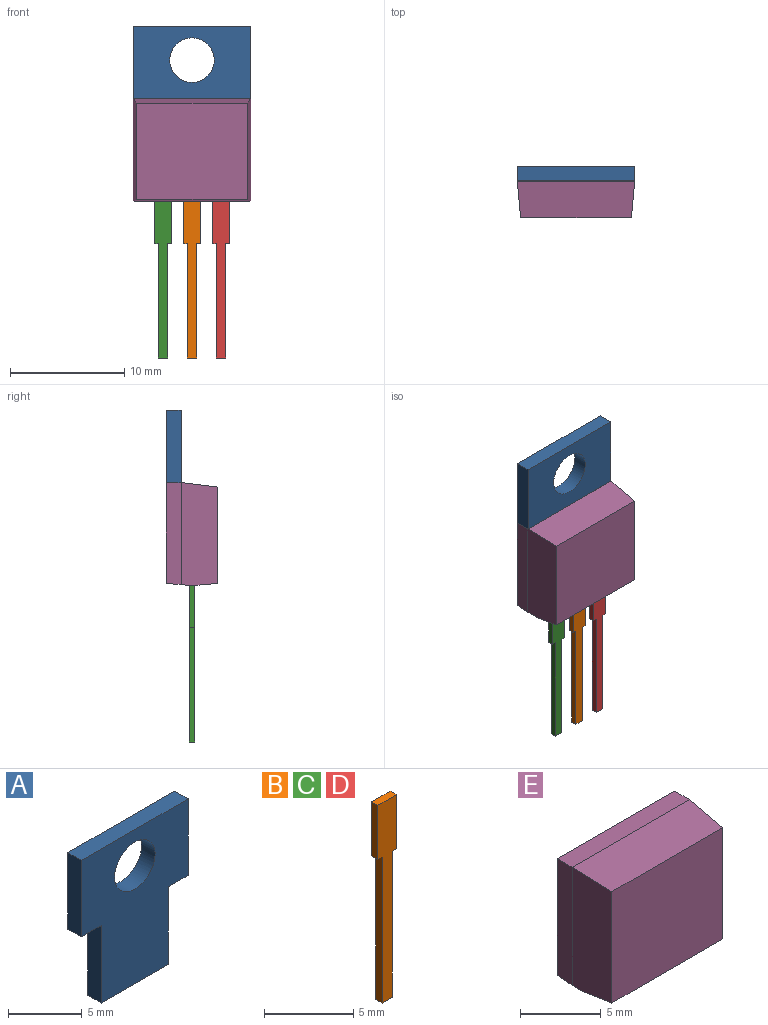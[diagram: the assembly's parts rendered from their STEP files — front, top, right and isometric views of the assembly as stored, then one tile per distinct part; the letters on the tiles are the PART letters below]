
ASSEMBLY  parts=5 mates=4
PART A: 11 faces, bbox 10.3x1.3x12.8 mm
  f0: plane 10.26x1.3mm, normal (0,0,1), area 13.3mm2, adj f1,f7,f8,f9
  f1: plane 6.35x1.3mm, normal (-1,0,0), area 8.3mm2, adj f0,f2,f8,f9
  f2: plane 1.91x1.3mm, normal (0,0,-1), area 2.5mm2, adj f1,f3,f8,f9
  f3: plane 6.45x1.3mm, normal (-1,0,0), area 8.4mm2, adj f2,f4,f8,f9
  f4: plane 6.44x1.3mm, normal (0,0,-1), area 8.4mm2, adj f3,f5,f8,f9
  f5: plane 6.45x1.3mm, normal (1,0,0), area 8.4mm2, adj f4,f6,f8,f9
  f6: plane 1.91x1.3mm, normal (0,0,-1), area 2.5mm2, adj f5,f7,f8,f9
  f7: plane 6.35x1.3mm, normal (1,0,0), area 8.3mm2, adj f0,f6,f8,f9
  f8: plane 12.8x10.26mm, normal (0,-1,0), area 94.8mm2, adj f0,f1,f2,f3,f4,f5,f6,f7
  f9: plane 12.8x10.26mm, normal (0,1,0), area 94.8mm2, adj f0,f1,f2,f3,f4,f5,f6,f7
  f10: cylinder r=1.95mm len=3.9mm, axis (0,1,0), area 15.9mm2, adj f8,f9
PART B: 10 faces, bbox 1.5x0.5x13.7 mm
  f0: plane 3.7x0.5mm, normal (-1,0,0), area 1.9mm2, adj f1,f7,f8,f9
  f1: plane 0.5x0.35mm, normal (0,0,-1), area 0.2mm2, adj f0,f2,f8,f9
  f2: plane 10x0.5mm, normal (-1,0,0), area 5mm2, adj f1,f3,f8,f9
  f3: plane 0.8x0.5mm, normal (0,0,-1), area 0.4mm2, adj f2,f4,f8,f9
  f4: plane 10x0.5mm, normal (1,0,0), area 5mm2, adj f3,f5,f8,f9
  f5: plane 0.5x0.35mm, normal (0,0,-1), area 0.2mm2, adj f4,f6,f8,f9
  f6: plane 3.7x0.5mm, normal (1,0,0), area 1.9mm2, adj f5,f7,f8,f9
  f7: plane 1.5x0.5mm, normal (0,0,1), area 0.8mm2, adj f0,f6,f8,f9
  f8: plane 13.7x1.5mm, normal (0,-1,0), area 13.6mm2, adj f0,f1,f2,f3,f4,f5,f6,f7
  f9: plane 13.7x1.5mm, normal (0,1,0), area 13.6mm2, adj f0,f1,f2,f3,f4,f5,f6,f7
PART C: same geometry as B
PART D: same geometry as B
PART E: 11 faces, bbox 10.3x4.5x9 mm
  f0: plane 8.94x1.3mm, normal (1,0,0), area 11.5mm2, adj f1,f5,f7,f9
  f1: plane 10.26x1.3mm, normal (0,0,1), area 13.3mm2, adj f0,f2,f5,f6
  f2: plane 8.94x1.3mm, normal (-1,0,0), area 11.5mm2, adj f1,f5,f8,f9
  f3: plane 10.14x0.5mm, normal (0,0,-1), area 5mm2, adj f7,f8,f9,f10
  f4: plane 9.7x8.43mm, normal (0,-1,0), area 81.8mm2, adj f6,f7,f8,f10
  f5: plane 10.26x8.83mm, normal (0,1,0), area 90.5mm2, adj f0,f1,f2,f9
  f6: plane 10.26x3.2mm, normal (0,-0.12,0.99), area 32.2mm2, adj f1,f4,f7,f8
  f7: plane 9x3.2mm, normal (1,-0.09,0), area 28.1mm2, adj f0,f3,f4,f6,f9,f10
  f8: plane 9x3.2mm, normal (-1,-0.09,0), area 28.1mm2, adj f2,f3,f4,f6,f9,f10
  f9: plane 10.26x2mm, normal (0,0.09,-1), area 20.6mm2, adj f0,f2,f3,f5,f7,f8
  f10: plane 10.05x2mm, normal (0,-0.09,-1), area 19.8mm2, adj f3,f4,f7,f8
PLACE A t=(30.13,0,-18.01)mm
PLACE B t=(41.01,-2,1.64)mm
PLACE C t=(38.47,-2,1.64)mm
PLACE D t=(43.55,-2,1.64)mm
PLACE E t=(30.13,0,-3.36)mm
MATE fastened E.f3 <-> C.f7  axis (0,0,-1) through (0,-2,-12.36)mm
MATE fastened A.f2 <-> E.f1  axis (0,0,1) through (0,0,-3.36)mm
MATE fastened E.f3 <-> B.f7  axis (0,0,-1) through (0,-2,-12.36)mm
MATE fastened E.f3 <-> D.f7  axis (0,0,-1) through (0,-2,-12.36)mm
